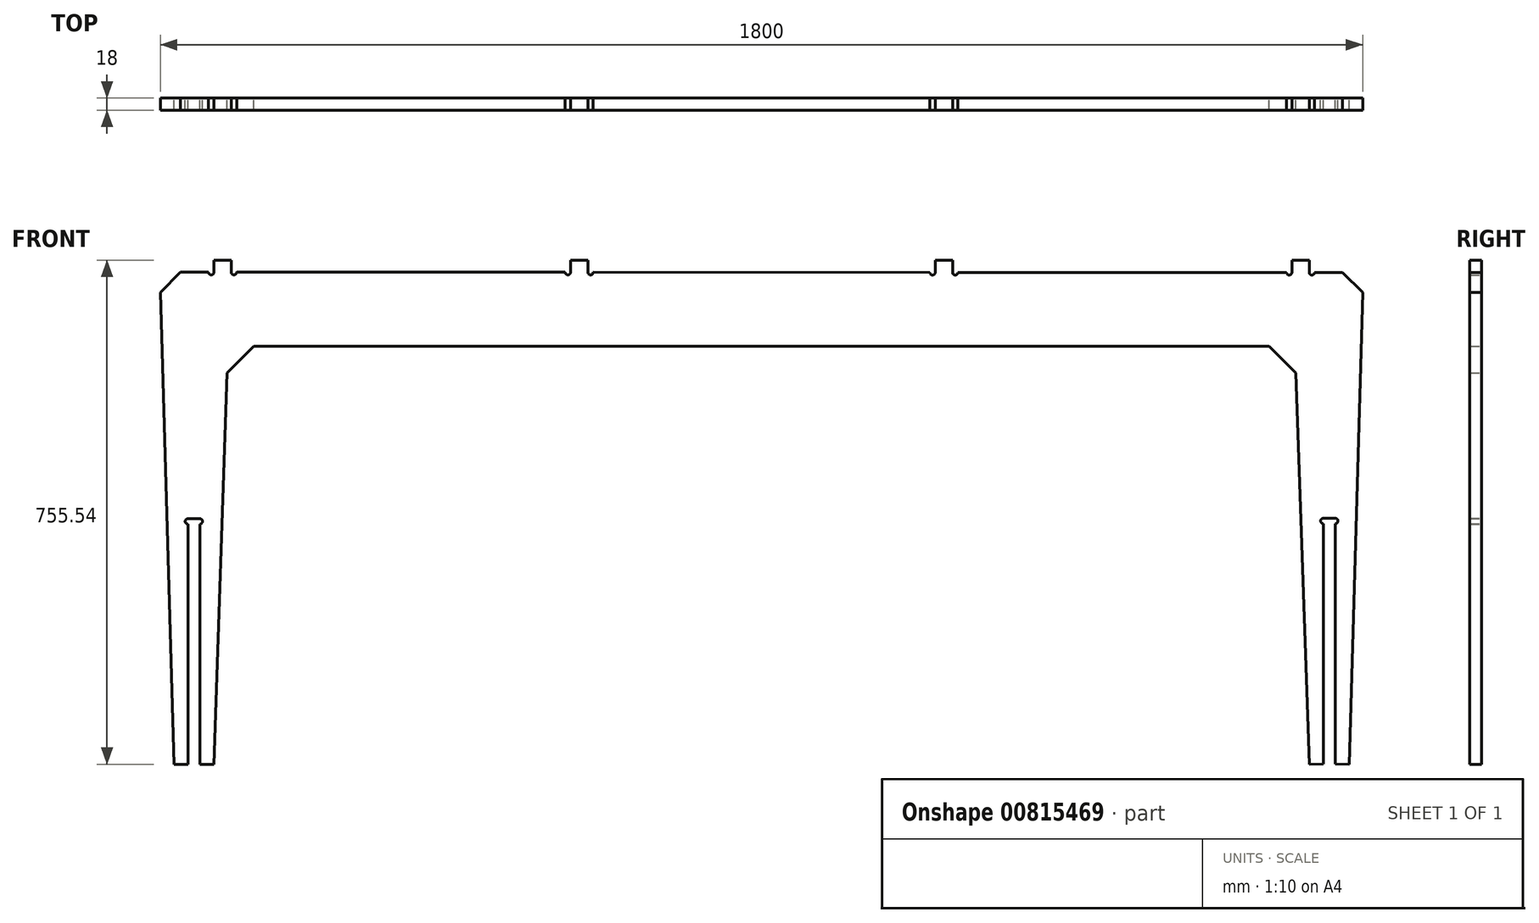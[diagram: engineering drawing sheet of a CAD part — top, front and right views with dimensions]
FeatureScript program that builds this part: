
annotation { "Feature Type Name" : "Feature", "Feature Type Description" : "" }
export const myFeature = defineFeature(function(context is Context, id is Id, definition is map)
    precondition{}
    {
        {
            var Q0;
            Q0=qCreatedBy(makeId("Front.planeOp"),FACE);
            var sketch = newSketch(context, id + "F0", { "sketchPlane" : qUnion([Q0])});
            skPoint(sketch, "E0.middle", {"position": v(0, 0) * mm});
            skLineSegment(sketch, "E1.right", {"start": v(1445, 379) * mm, "end": v(1445, 361) * mm});
            skPoint(sketch, "E2.start.orphan", {"position": v(-195, 368.73) * mm});
            skPoint(sketch, "E3.start.orphan", {"position": v(1445, 370) * mm});
            skLineSegment(sketch, "E4", {"start": v(-203, 361.18) * mm, "end": v(-244.9, 361.18) * mm});
            skPoint(sketch, "E5.orphan", {"position": v(-274.99, 376.28) * mm});
            skLineSegment(sketch, "E6", {"start": v(1453, 361) * mm, "end": v(1494.9, 361) * mm});
            skPoint(sketch, "E7.orphan", {"position": v(274.99, 376.28) * mm});
            skArc(sketch, "E8", {"start": v(1445, 361) * mm, "mid": v(1449, 357) * mm, "end": v(1453, 361) * mm});
            skArc(sketch, "E9", {"start": v(-203, 361.18) * mm, "mid": v(-199, 357.18) * mm, "end": v(-195, 361.18) * mm});
            skLineSegment(sketch, "E10.top", {"start": v(-244.9, 361.18) * mm, "end": v(-203, 361.18) * mm});
            skLineSegment(sketch, "E11", {"start": v(-244.9, 361.18) * mm, "end": v(-274.99, 331.07) * mm});
            skLineSegment(sketch, "E12", {"start": v(-134.99, 250.34) * mm, "end": v(-174.99, 210.34) * mm});
            skLineSegment(sketch, "E13", {"start": v(1385.01, 250.34) * mm, "end": v(1425.01, 210.34) * mm});
            skLineSegment(sketch, "E14", {"start": v(-274.99, 331.07) * mm, "end": v(-254.99, -376.28) * mm});
            skLineSegment(sketch, "E15", {"start": v(-174.99, 210.34) * mm, "end": v(-194.99, -376.28) * mm});
            skPoint(sketch, "E16.start.orphan", {"position": v(-274.99, -376.28) * mm});
            skLineSegment(sketch, "E17", {"start": v(1425.01, 210.34) * mm, "end": v(1445.01, -376.28) * mm});
            skLineSegment(sketch, "E18", {"start": v(1525.01, 331) * mm, "end": v(1505.01, -376.36) * mm});
            skPoint(sketch, "E19.start.orphan", {"position": v(274.99, -376.28) * mm});
            skPoint(sketch, "E20.left.end.orphan", {"position": v(-195, 361.18) * mm});
            skPoint(sketch, "E21.orphan", {"position": v(-195, 376.28) * mm});
            skLineSegment(sketch, "E22", {"start": v(-195, 361.18) * mm, "end": v(-195, 379.18) * mm});
            skLineSegment(sketch, "E23", {"start": v(-195, 379.18) * mm, "end": v(-169, 379.18) * mm});
            skLineSegment(sketch, "E24", {"start": v(-169, 379.18) * mm, "end": v(-169, 361.18) * mm});
            skLineSegment(sketch, "E25", {"start": v(-254.99, -376.28) * mm, "end": v(-233.99, -376.28) * mm});
            skLineSegment(sketch, "E26.top", {"start": v(-233.99, -8.28) * mm, "end": v(-215.99, -8.28) * mm});
            skLineSegment(sketch, "E26.left", {"start": v(-233.99, -376.28) * mm, "end": v(-233.99, -16.28) * mm});
            skLineSegment(sketch, "E26.right", {"start": v(-215.99, -376.28) * mm, "end": v(-215.99, -16.28) * mm});
            skLineSegment(sketch, "E27.top", {"start": v(-233.99, 361.18) * mm, "end": v(-215.99, 361.18) * mm});
            skLineSegment(sketch, "E28", {"start": v(1505.01, -376.36) * mm, "end": v(1484.02, -375.76) * mm});
            skLineSegment(sketch, "E29.top", {"start": v(1484.02, -7.69) * mm, "end": v(1466.02, -7.69) * mm});
            skLineSegment(sketch, "E29.left", {"start": v(1484.02, -375.76) * mm, "end": v(1484.02, -15.69) * mm});
            skLineSegment(sketch, "E29.right", {"start": v(1466.02, -375.69) * mm, "end": v(1466.02, -15.69) * mm});
            skLineSegment(sketch, "E30.top", {"start": v(1494.9, 361) * mm, "end": v(1466.02, 361) * mm});
            skLineSegment(sketch, "E31", {"start": v(1445, 379) * mm, "end": v(1419, 379) * mm});
            skLineSegment(sketch, "E32", {"start": v(1419, 379) * mm, "end": v(1419, 361) * mm});
            skArc(sketch, "E33", {"start": v(-169, 361.18) * mm, "mid": v(-165, 357.18) * mm, "end": v(-161, 361.18) * mm});
            skLineSegment(sketch, "E34", {"start": v(-215.99, -376.28) * mm, "end": v(-194.99, -376.28) * mm});
            skLineSegment(sketch, "E35", {"start": v(1445.01, -376.28) * mm, "end": v(1466.02, -375.69) * mm});
            skArc(sketch, "E36", {"start": v(1411, 361) * mm, "mid": v(1415, 357) * mm, "end": v(1419, 361) * mm});
            skLineSegment(sketch, "E37", {"start": v(-274.99, 331.07) * mm, "end": v(-274.99, 376.28) * mm});
            skLineSegment(sketch, "E38", {"start": v(-134.99, 250.34) * mm, "end": v(1385.01, 250.34) * mm});
            skLineSegment(sketch, "E39", {"start": v(-161, 361.18) * mm, "end": v(331, 361.18) * mm});
            skLineSegment(sketch, "E40", {"start": v(1411, 361) * mm, "end": v(919, 361) * mm});
            skLineSegment(sketch, "E41.top", {"start": v(911, 379) * mm, "end": v(885, 379) * mm});
            skLineSegment(sketch, "E41.left", {"start": v(911, 361) * mm, "end": v(911, 379) * mm});
            skLineSegment(sketch, "E41.right", {"start": v(885, 361) * mm, "end": v(885, 379) * mm});
            skLineSegment(sketch, "E42.top", {"start": v(339, 379.18) * mm, "end": v(365, 379.18) * mm});
            skLineSegment(sketch, "E42.left", {"start": v(339, 361.18) * mm, "end": v(339, 379.18) * mm});
            skLineSegment(sketch, "E42.right", {"start": v(365, 361.18) * mm, "end": v(365, 379.18) * mm});
            skArc(sketch, "E43", {"start": v(331, 361.18) * mm, "mid": v(335, 357.18) * mm, "end": v(339, 361.18) * mm});
            skArc(sketch, "E44", {"start": v(365, 361.18) * mm, "mid": v(369, 357.17) * mm, "end": v(373, 361.17) * mm});
            skLineSegment(sketch, "E45.trimOffspring", {"start": v(373, 361.17) * mm, "end": v(877, 361) * mm});
            skArc(sketch, "E46", {"start": v(911, 361) * mm, "mid": v(915, 357) * mm, "end": v(919, 361) * mm});
            skArc(sketch, "E47", {"start": v(877, 361) * mm, "mid": v(881, 357) * mm, "end": v(885, 361) * mm});
            skArc(sketch, "E48", {"start": v(-233.99, -8.28) * mm, "mid": v(-237.99, -12.28) * mm, "end": v(-233.99, -16.28) * mm});
            skArc(sketch, "E49", {"start": v(-215.99, -16.28) * mm, "mid": v(-211.99, -12.28) * mm, "end": v(-215.99, -8.28) * mm});
            skArc(sketch, "E50", {"start": v(1484.02, -15.69) * mm, "mid": v(1488.02, -11.69) * mm, "end": v(1484.02, -7.69) * mm});
            skArc(sketch, "E51", {"start": v(1466.02, -7.69) * mm, "mid": v(1462.02, -11.69) * mm, "end": v(1466.02, -15.69) * mm});
            skLineSegment(sketch, "E52", {"start": v(1525.01, 331) * mm, "end": v(1525.01, 421.85) * mm});
            skLineSegment(sketch, "E53", {"start": v(1494.9, 361) * mm, "end": v(1525.01, 331) * mm});
            skSolve(sketch);
        }
        {
            var Q0;
            Q0=makeQuery(id+"F0.imprint","IMPRINT",FACE,{"disambiguationData":[TD([[makeQuery(id+"F0.imprint","IMPRINT",EDGE,{"derivedFrom":sQuery(id+"F0.wireOp",EDGE,"E1.right")}),-1.0]])]});
            extrude(context, id + "F1", {"entities" : qUnion([Q0]), "depth" : 18 * mm, "offsetDistance" : 25 * mm});
        }
    });
